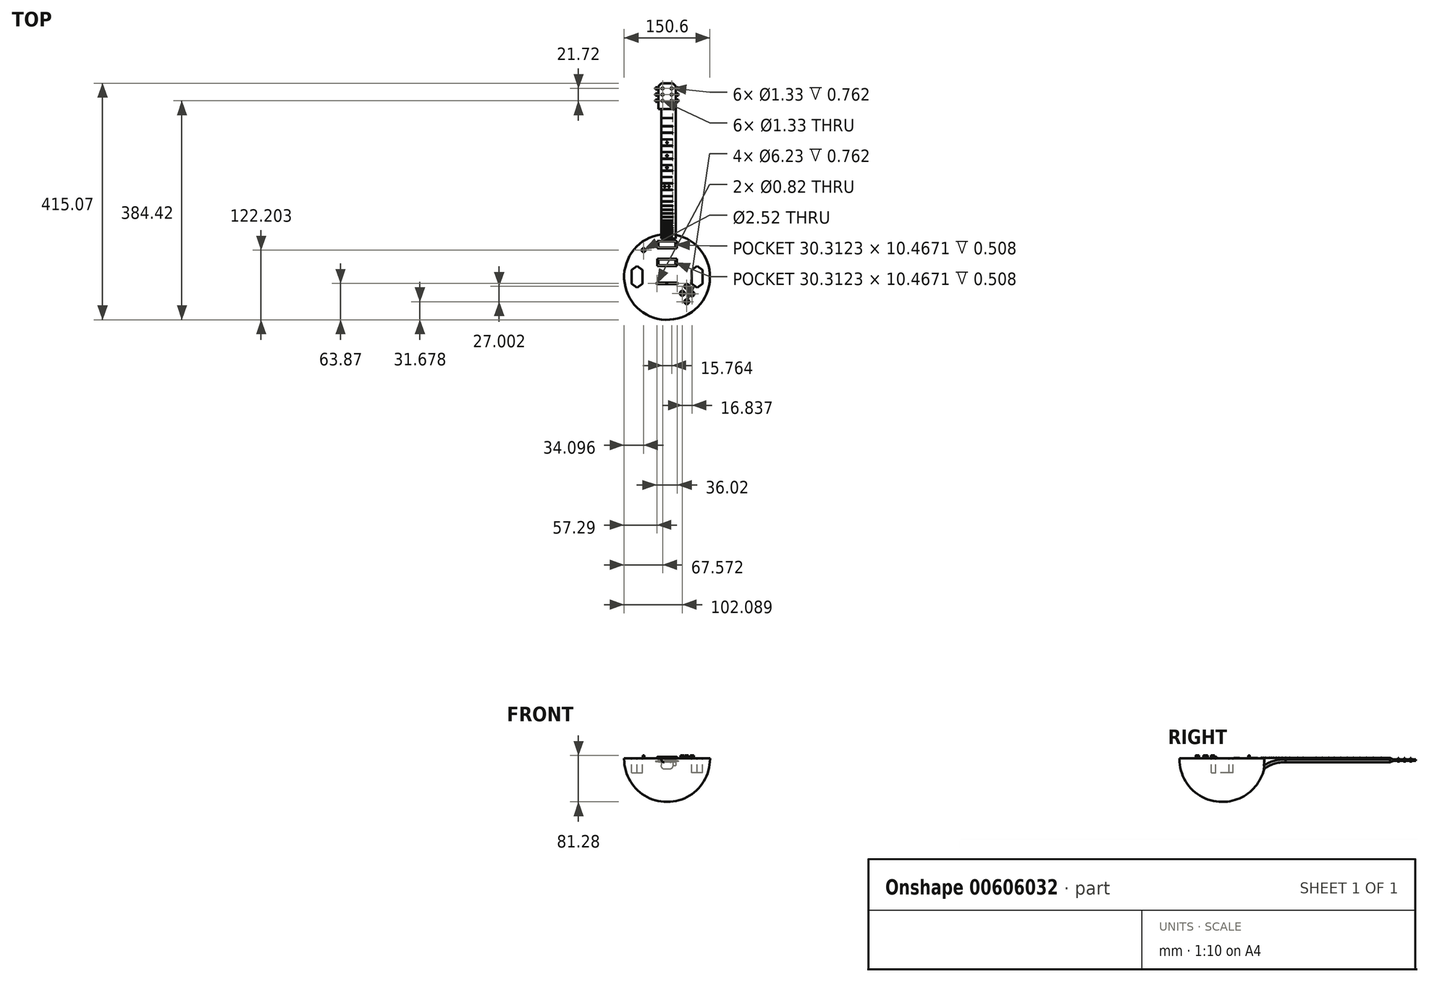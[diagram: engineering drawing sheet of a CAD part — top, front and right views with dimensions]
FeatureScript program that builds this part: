
annotation { "Feature Type Name" : "Feature", "Feature Type Description" : "" }
export const myFeature = defineFeature(function(context is Context, id is Id, definition is map)
    precondition{}
    {
        {
            var Q0;
            Q0=qCreatedBy(makeId("Top.planeOp"),FACE);
            var sketch = newSketch(context, id + "F0", { "sketchPlane" : qUnion([Q0])});
            skCircle(sketch, "E0", {"center": v(0, 0) * mm, "radius": 75.3 * mm});
            skSolve(sketch);
        }
        {
            var Q0;
            Q0 = qSketchRegion(id + "F0", true);
            extrude(context, id + "F1", {"entities" : qUnion([Q0]), "oppositeDirection" : true, "depth" : 76.2 * mm, "offsetDistance" : 25.4 * mm});
        }
        {
            var Q0;
            Q0=makeQuery(id+"F1.opExtrude","CAP_EDGE",EDGE,{"disambiguationData":[OSD([sQuery(id+"F0.wireOp",EDGE,"E0")])],"isStart":false});
            fillet(context, id + "F2", {"entities" : qUnion([Q0]), "radius" : 74.93 * mm, "tangentPropagation" : true, "allowEdgeOverflow" : false});
        }
        {
            var Q0;
            Q0=makeQuery(id+"F1.opExtrude","CAP_FACE",FACE,{"disambiguationData":[OSD([sQuery(id+"F0.wireOp",EDGE,"E0")])],"isStart":true});
            var sketch = newSketch(context, id + "F3", { "sketchPlane" : qUnion([Q0])});
            skCircle(sketch, "E1.0", {"center": v(0, 0) * mm, "radius": 75.3 * mm});
            skLineSegment(sketch, "E2", {"start": v(0, 0) * mm, "end": v(-75.3, 0) * mm, "construction": true});
            skLineSegment(sketch, "E3", {"start": v(0, 0) * mm, "end": v(75.3, 0) * mm, "construction": true});
            skLineSegment(sketch, "E4", {"start": v(0, 0) * mm, "end": v(0, 75.3) * mm, "construction": true});
            skLineSegment(sketch, "E5", {"start": v(0, 0) * mm, "end": v(0, -75.3) * mm, "construction": true});
            skLineSegment(sketch, "E6", {"start": v(-62.04, 0) * mm, "end": v(-62.04, 11.91) * mm});
            skLineSegment(sketch, "E7", {"start": v(-62.04, 11.91) * mm, "end": v(-52.65, 18.94) * mm});
            skLineSegment(sketch, "E8", {"start": v(-52.65, 18.94) * mm, "end": v(-43.25, 11.91) * mm});
            skLineSegment(sketch, "E9", {"start": v(-43.25, 11.91) * mm, "end": v(-43.25, 0) * mm});
            skLineSegment(sketch, "E10.MirrorCS", {"start": v(-43.25, -11.91) * mm, "end": v(-43.25, 0) * mm});
            skLineSegment(sketch, "E11.MirrorCS", {"start": v(-52.65, -18.94) * mm, "end": v(-43.25, -11.91) * mm});
            skLineSegment(sketch, "E12.MirrorCS", {"start": v(-62.04, -11.91) * mm, "end": v(-52.65, -18.94) * mm});
            skLineSegment(sketch, "E13.MirrorCS", {"start": v(-62.04, 0) * mm, "end": v(-62.04, -11.91) * mm});
            skLineSegment(sketch, "E14.MirrorCS", {"start": v(43.25, 11.91) * mm, "end": v(43.25, 0) * mm});
            skLineSegment(sketch, "E15.MirrorCS", {"start": v(52.65, 18.94) * mm, "end": v(43.25, 11.91) * mm});
            skLineSegment(sketch, "E16.MirrorCS", {"start": v(62.04, 11.91) * mm, "end": v(52.65, 18.94) * mm});
            skLineSegment(sketch, "E17.MirrorCS", {"start": v(62.04, 0) * mm, "end": v(62.04, 11.91) * mm});
            skLineSegment(sketch, "E18.MirrorCS", {"start": v(62.04, 0) * mm, "end": v(62.04, -11.91) * mm});
            skLineSegment(sketch, "E19.MirrorCS", {"start": v(43.25, -11.91) * mm, "end": v(43.25, 0) * mm});
            skLineSegment(sketch, "E20.MirrorCS", {"start": v(52.65, -18.94) * mm, "end": v(43.25, -11.91) * mm});
            skLineSegment(sketch, "E21.MirrorCS", {"start": v(62.04, -11.91) * mm, "end": v(52.65, -18.94) * mm});
            skLineSegment(sketch, "E22", {"start": v(0, 63) * mm, "end": v(17.31, 63) * mm});
            skLineSegment(sketch, "E23", {"start": v(17.31, 63) * mm, "end": v(17.31, 50.39) * mm});
            skLineSegment(sketch, "E24", {"start": v(17.31, 50.39) * mm, "end": v(0, 50.39) * mm});
            skLineSegment(sketch, "E25", {"start": v(0, 50.39) * mm, "end": v(-17.31, 50.39) * mm});
            skLineSegment(sketch, "E26", {"start": v(-17.31, 50.39) * mm, "end": v(-17.31, 63) * mm});
            skLineSegment(sketch, "E27", {"start": v(-17.31, 63) * mm, "end": v(0, 63) * mm});
            skLineSegment(sketch, "E28", {"start": v(-15.36, 51.52) * mm, "end": v(-15.36, 61.98) * mm});
            skLineSegment(sketch, "E29", {"start": v(-15.36, 61.98) * mm, "end": v(14.95, 61.98) * mm});
            skLineSegment(sketch, "E30", {"start": v(14.95, 61.98) * mm, "end": v(14.95, 51.52) * mm});
            skLineSegment(sketch, "E31", {"start": v(14.95, 51.52) * mm, "end": v(-15.36, 51.52) * mm});
            skCircle(sketch, "E32", {"center": v(-16.46, 60.98) * mm, "radius": 0.48 * mm});
            skCircle(sketch, "E33", {"center": v(-16.46, 57.1) * mm, "radius": 0.48 * mm});
            skCircle(sketch, "E34", {"center": v(-16.46, 52.33) * mm, "radius": 0.48 * mm});
            skCircle(sketch, "E35", {"center": v(16.04, 60.98) * mm, "radius": 0.48 * mm});
            skCircle(sketch, "E36", {"center": v(16.04, 57.1) * mm, "radius": 0.48 * mm});
            skCircle(sketch, "E37", {"center": v(16.04, 52.33) * mm, "radius": 0.48 * mm});
            skLineSegment(sketch, "E38", {"start": v(0, 31.55) * mm, "end": v(17.31, 31.55) * mm});
            skLineSegment(sketch, "E39", {"start": v(17.31, 31.55) * mm, "end": v(17.31, 18.94) * mm});
            skLineSegment(sketch, "E40", {"start": v(17.31, 18.94) * mm, "end": v(0, 18.94) * mm});
            skLineSegment(sketch, "E41", {"start": v(0, 18.94) * mm, "end": v(-17.31, 18.94) * mm});
            skLineSegment(sketch, "E42", {"start": v(-17.31, 18.94) * mm, "end": v(-17.31, 31.55) * mm});
            skLineSegment(sketch, "E43", {"start": v(-17.31, 31.55) * mm, "end": v(0, 31.55) * mm});
            skLineSegment(sketch, "E44", {"start": v(-15.36, 20.07) * mm, "end": v(-15.36, 30.53) * mm});
            skLineSegment(sketch, "E45", {"start": v(-15.36, 30.53) * mm, "end": v(14.95, 30.53) * mm});
            skLineSegment(sketch, "E46", {"start": v(14.95, 30.53) * mm, "end": v(14.95, 20.07) * mm});
            skLineSegment(sketch, "E47", {"start": v(14.95, 20.07) * mm, "end": v(-15.36, 20.07) * mm});
            skCircle(sketch, "E48", {"center": v(-16.46, 29.53) * mm, "radius": 0.48 * mm});
            skCircle(sketch, "E49", {"center": v(-16.46, 25.65) * mm, "radius": 0.48 * mm});
            skCircle(sketch, "E50", {"center": v(-16.46, 20.88) * mm, "radius": 0.48 * mm});
            skCircle(sketch, "E51", {"center": v(16.04, 29.53) * mm, "radius": 0.48 * mm});
            skCircle(sketch, "E52", {"center": v(16.04, 25.65) * mm, "radius": 0.48 * mm});
            skCircle(sketch, "E53", {"center": v(16.04, 20.88) * mm, "radius": 0.48 * mm});
            skLineSegment(sketch, "E54", {"start": v(0, -9.89) * mm, "end": v(17.31, -9.89) * mm});
            skLineSegment(sketch, "E55", {"start": v(17.31, -9.89) * mm, "end": v(17.31, -12.97) * mm});
            skLineSegment(sketch, "E56", {"start": v(17.31, -12.97) * mm, "end": v(0, -12.97) * mm});
            skLineSegment(sketch, "E57.MirrorCS", {"start": v(-17.31, -12.97) * mm, "end": v(0, -12.97) * mm});
            skLineSegment(sketch, "E58.MirrorCS", {"start": v(0, -9.89) * mm, "end": v(-17.31, -9.89) * mm});
            skLineSegment(sketch, "E59.MirrorCS", {"start": v(-17.31, -9.89) * mm, "end": v(-17.31, -12.97) * mm});
            skArc(sketch, "E60", {"start": v(-17.31, -9.89) * mm, "mid": v(-18.85, -11.43) * mm, "end": v(-17.31, -12.97) * mm});
            skArc(sketch, "E61.MirrorCS", {"start": v(17.31, -9.89) * mm, "mid": v(18.85, -11.43) * mm, "end": v(17.31, -12.97) * mm});
            skCircle(sketch, "E62", {"center": v(-18, -11.43) * mm, "radius": 0.41 * mm});
            skCircle(sketch, "E63.MirrorC", {"center": v(18, -11.43) * mm, "radius": 0.41 * mm});
            skCircle(sketch, "E64", {"center": v(34.62, -16.62) * mm, "radius": 4.23 * mm});
            skCircle(sketch, "E65", {"center": v(26.79, -28.94) * mm, "radius": 4.23 * mm});
            skCircle(sketch, "E66", {"center": v(43.63, -29.8) * mm, "radius": 4.23 * mm});
            skCircle(sketch, "E67", {"center": v(34.56, -43.62) * mm, "radius": 4.23 * mm});
            skCircle(sketch, "E68", {"center": v(34.62, -16.62) * mm, "radius": 3.12 * mm});
            skCircle(sketch, "E69", {"center": v(26.79, -28.94) * mm, "radius": 3.12 * mm});
            skCircle(sketch, "E70", {"center": v(43.63, -29.8) * mm, "radius": 3.12 * mm});
            skCircle(sketch, "E71", {"center": v(34.56, -43.62) * mm, "radius": 3.12 * mm});
            skCircle(sketch, "E72", {"center": v(-41.2, 46.9) * mm, "radius": 3.4 * mm});
            skCircle(sketch, "E73", {"center": v(-41.2, 46.9) * mm, "radius": 1.26 * mm});
            skSolve(sketch);
        }
        {
            var Q0;
            Q0=makeQuery(id+"F3.imprint","IMPRINT",FACE,{"disambiguationData":[TD([[makeQuery(id+"F3.imprint","IMPRINT",EDGE,{"derivedFrom":sQuery(id+"F3.wireOp",EDGE,"E6")}),-1.0]])]});
            var Q1;
            Q1=makeQuery(id+"F3.imprint","IMPRINT",FACE,{"disambiguationData":[TD([[makeQuery(id+"F3.imprint","IMPRINT",EDGE,{"derivedFrom":sQuery(id+"F3.wireOp",EDGE,"E14.MirrorCS")}),1.0]])]});
            extrude(context, id + "F4", {"entities" : qUnion([Q0, Q1]), "operationType" : NewBodyOperationType.REMOVE, "oppositeDirection" : true, "depth" : 25.4 * mm, "offsetDistance" : 25.4 * mm});
        }
        {
            var Q0;
            Q0=makeQuery(id+"F3.imprint","IMPRINT",FACE,{"disambiguationData":[TD([[makeQuery(id+"F3.imprint","IMPRINT",EDGE,{"derivedFrom":sQuery(id+"F3.wireOp",EDGE,"E22")}),-1.0]])]});
            var Q1;
            Q1=makeQuery(id+"F3.imprint","IMPRINT",FACE,{"disambiguationData":[TD([[makeQuery(id+"F3.imprint","IMPRINT",EDGE,{"derivedFrom":sQuery(id+"F3.wireOp",EDGE,"E38")}),-1.0]])]});
            extrude(context, id + "F5", {"entities" : qUnion([Q0, Q1]), "depth" : 0.5 * mm, "offsetDistance" : 25.4 * mm});
        }
        {
            var Q0;
            Q0=makeQuery(id+"F3.imprint","IMPRINT",FACE,{"disambiguationData":[TD([[makeQuery(id+"F3.imprint","IMPRINT",EDGE,{"derivedFrom":sQuery(id+"F3.wireOp",EDGE,"E32")}),1.0]])]});
            extrude(context, id + "F6", {"entities" : qUnion([Q0]), "depth" : 0.76 * mm, "offsetDistance" : 25.4 * mm});
        }
        {
            var Q0;
            Q0=makeQuery(id+"F3.imprint","IMPRINT",FACE,{"disambiguationData":[TD([[makeQuery(id+"F3.imprint","IMPRINT",EDGE,{"derivedFrom":sQuery(id+"F3.wireOp",EDGE,"E33")}),1.0]])]});
            var Q1;
            Q1=makeQuery(id+"F3.imprint","IMPRINT",FACE,{"disambiguationData":[TD([[makeQuery(id+"F3.imprint","IMPRINT",EDGE,{"derivedFrom":sQuery(id+"F3.wireOp",EDGE,"E34")}),1.0]])]});
            var Q2;
            Q2=makeQuery(id+"F3.imprint","IMPRINT",FACE,{"disambiguationData":[TD([[makeQuery(id+"F3.imprint","IMPRINT",EDGE,{"derivedFrom":sQuery(id+"F3.wireOp",EDGE,"E35")}),1.0]])]});
            var Q3;
            Q3=makeQuery(id+"F3.imprint","IMPRINT",FACE,{"disambiguationData":[TD([[makeQuery(id+"F3.imprint","IMPRINT",EDGE,{"derivedFrom":sQuery(id+"F3.wireOp",EDGE,"E36")}),1.0]])]});
            var Q4;
            Q4=makeQuery(id+"F3.imprint","IMPRINT",FACE,{"disambiguationData":[TD([[makeQuery(id+"F3.imprint","IMPRINT",EDGE,{"derivedFrom":sQuery(id+"F3.wireOp",EDGE,"E37")}),1.0]])]});
            var Q5;
            Q5=makeQuery(id+"F3.imprint","IMPRINT",FACE,{"disambiguationData":[TD([[makeQuery(id+"F3.imprint","IMPRINT",EDGE,{"derivedFrom":sQuery(id+"F3.wireOp",EDGE,"E48")}),1.0]])]});
            var Q6;
            Q6=makeQuery(id+"F3.imprint","IMPRINT",FACE,{"disambiguationData":[TD([[makeQuery(id+"F3.imprint","IMPRINT",EDGE,{"derivedFrom":sQuery(id+"F3.wireOp",EDGE,"E49")}),1.0]])]});
            var Q7;
            Q7=makeQuery(id+"F3.imprint","IMPRINT",FACE,{"disambiguationData":[TD([[makeQuery(id+"F3.imprint","IMPRINT",EDGE,{"derivedFrom":sQuery(id+"F3.wireOp",EDGE,"E50")}),1.0]])]});
            var Q8;
            Q8=makeQuery(id+"F3.imprint","IMPRINT",FACE,{"disambiguationData":[TD([[makeQuery(id+"F3.imprint","IMPRINT",EDGE,{"derivedFrom":sQuery(id+"F3.wireOp",EDGE,"E51")}),1.0]])]});
            var Q9;
            Q9=makeQuery(id+"F3.imprint","IMPRINT",FACE,{"disambiguationData":[TD([[makeQuery(id+"F3.imprint","IMPRINT",EDGE,{"derivedFrom":sQuery(id+"F3.wireOp",EDGE,"E52")}),1.0]])]});
            var Q10;
            Q10=makeQuery(id+"F3.imprint","IMPRINT",FACE,{"disambiguationData":[TD([[makeQuery(id+"F3.imprint","IMPRINT",EDGE,{"derivedFrom":sQuery(id+"F3.wireOp",EDGE,"E53")}),1.0]])]});
            extrude(context, id + "F7", {"entities" : qUnion([Q0, Q1, Q2, Q3, Q4, Q5, Q6, Q7, Q8, Q9, Q10]), "operationType" : NewBodyOperationType.ADD, "depth" : 0.76 * mm, "offsetDistance" : 25.4 * mm});
        }
        {
            var Q0;
            Q0=makeQuery(id+"F3.imprint","IMPRINT",FACE,{"disambiguationData":[TD([[makeQuery(id+"F3.imprint","IMPRINT",EDGE,{"derivedFrom":sQuery(id+"F3.wireOp",EDGE,"E44")}),-1.0]])]});
            var Q1;
            Q1=makeQuery(id+"F3.imprint","IMPRINT",FACE,{"disambiguationData":[TD([[makeQuery(id+"F3.imprint","IMPRINT",EDGE,{"derivedFrom":sQuery(id+"F3.wireOp",EDGE,"E28")}),-1.0]])]});
            extrude(context, id + "F8", {"entities" : qUnion([Q0, Q1]), "depth" : 1.02 * mm, "offsetDistance" : 25.4 * mm});
        }
        {
            var Q0;
            Q0=makeQuery(id+"F3.imprint","IMPRINT",FACE,{"disambiguationData":[TD([[makeQuery(id+"F3.imprint","IMPRINT",EDGE,{"derivedFrom":sQuery(id+"F3.wireOp",EDGE,"E54")}),-1.0]])]});
            extrude(context, id + "F9", {"entities" : qUnion([Q0]), "depth" : 2.54 * mm, "offsetDistance" : 25.4 * mm});
        }
        {
            var Q0;
            Q0=makeQuery(id+"F9.opExtrude","CAP_EDGE",EDGE,{"disambiguationData":[OSD([sQuery(id+"F3.wireOp",EDGE,"E56"),sQuery(id+"F3.wireOp",EDGE,"E57.MirrorCS")])],"isStart":false});
            fillet(context, id + "F10", {"entities" : qUnion([Q0]), "radius" : 3.05 * mm, "tangentPropagation" : true, "allowEdgeOverflow" : false});
        }
        {
            var Q0;
            Q0=makeQuery(id+"F3.imprint","IMPRINT",FACE,{"disambiguationData":[TD([[makeQuery(id+"F3.imprint","IMPRINT",EDGE,{"derivedFrom":sQuery(id+"F3.wireOp",EDGE,"E59.MirrorCS")}),-1.0]])]});
            var Q1;
            Q1=makeQuery(id+"F3.imprint","IMPRINT",FACE,{"disambiguationData":[TD([[makeQuery(id+"F3.imprint","IMPRINT",EDGE,{"derivedFrom":sQuery(id+"F3.wireOp",EDGE,"E55")}),1.0]])]});
            extrude(context, id + "F11", {"entities" : qUnion([Q0, Q1]), "depth" : 0.5 * mm, "offsetDistance" : 25.4 * mm});
        }
        {
            var Q0;
            Q0=makeQuery(id+"F3.imprint","IMPRINT",FACE,{"disambiguationData":[TD([[makeQuery(id+"F3.imprint","IMPRINT",EDGE,{"derivedFrom":sQuery(id+"F3.wireOp",EDGE,"E65")}),1.0]])]});
            var Q1;
            Q1=makeQuery(id+"F3.imprint","IMPRINT",FACE,{"disambiguationData":[TD([[makeQuery(id+"F3.imprint","IMPRINT",EDGE,{"derivedFrom":sQuery(id+"F3.wireOp",EDGE,"E64")}),1.0]])]});
            var Q2;
            Q2=makeQuery(id+"F3.imprint","IMPRINT",FACE,{"disambiguationData":[TD([[makeQuery(id+"F3.imprint","IMPRINT",EDGE,{"derivedFrom":sQuery(id+"F3.wireOp",EDGE,"E66")}),1.0]])]});
            var Q3;
            Q3=makeQuery(id+"F3.imprint","IMPRINT",FACE,{"disambiguationData":[TD([[makeQuery(id+"F3.imprint","IMPRINT",EDGE,{"derivedFrom":sQuery(id+"F3.wireOp",EDGE,"E67")}),1.0]])]});
            extrude(context, id + "F12", {"entities" : qUnion([Q0, Q1, Q2, Q3]), "depth" : 0.76 * mm, "offsetDistance" : 25.4 * mm});
        }
        {
            var Q0;
            Q0=makeQuery(id+"F3.imprint","IMPRINT",FACE,{"disambiguationData":[TD([[makeQuery(id+"F3.imprint","IMPRINT",EDGE,{"derivedFrom":sQuery(id+"F3.wireOp",EDGE,"E69")}),1.0]])]});
            var Q1;
            Q1=makeQuery(id+"F3.imprint","IMPRINT",FACE,{"disambiguationData":[TD([[makeQuery(id+"F3.imprint","IMPRINT",EDGE,{"derivedFrom":sQuery(id+"F3.wireOp",EDGE,"E68")}),1.0]])]});
            var Q2;
            Q2=makeQuery(id+"F3.imprint","IMPRINT",FACE,{"disambiguationData":[TD([[makeQuery(id+"F3.imprint","IMPRINT",EDGE,{"derivedFrom":sQuery(id+"F3.wireOp",EDGE,"E70")}),1.0]])]});
            var Q3;
            Q3=makeQuery(id+"F3.imprint","IMPRINT",FACE,{"disambiguationData":[TD([[makeQuery(id+"F3.imprint","IMPRINT",EDGE,{"derivedFrom":sQuery(id+"F3.wireOp",EDGE,"E71")}),1.0]])]});
            extrude(context, id + "F13", {"entities" : qUnion([Q0, Q1, Q2, Q3]), "depth" : 5.08 * mm, "offsetDistance" : 25.4 * mm});
        }
        {
            var Q0;
            Q0=makeQuery(id+"F3.imprint","IMPRINT",FACE,{"disambiguationData":[TD([[makeQuery(id+"F3.imprint","IMPRINT",EDGE,{"derivedFrom":sQuery(id+"F3.wireOp",EDGE,"E72")}),1.0]])]});
            extrude(context, id + "F14", {"entities" : qUnion([Q0]), "depth" : 0.76 * mm, "offsetDistance" : 25.4 * mm});
        }
        {
            var Q0;
            Q0=makeQuery(id+"F3.imprint","IMPRINT",FACE,{"disambiguationData":[TD([[makeQuery(id+"F3.imprint","IMPRINT",EDGE,{"derivedFrom":sQuery(id+"F3.wireOp",EDGE,"E73")}),1.0]])]});
            extrude(context, id + "F15", {"entities" : qUnion([Q0]), "depth" : 5.08 * mm, "offsetDistance" : 25.4 * mm});
        }
        {
            var Q0;
            Q0=makeQuery(id+"F15.opExtrude","CAP_EDGE",EDGE,{"disambiguationData":[OSD([sQuery(id+"F3.wireOp",EDGE,"E73")])],"isStart":false});
            fillet(context, id + "F16", {"entities" : qUnion([Q0]), "radius" : 0.5 * mm, "tangentPropagation" : true, "allowEdgeOverflow" : false});
        }
        {
            var Q0;
            Q0=qCreatedBy(makeId("Right.planeOp"),FACE);
            var sketch = newSketch(context, id + "F17", { "sketchPlane" : qUnion([Q0])});
            skLineSegment(sketch, "E74", {"start": v(67.16, 0) * mm, "end": v(294.63, 0) * mm});
            skArc(sketch, "E75", {"start": v(110.96, -6.75) * mm, "mid": v(85.61, -11.39) * mm, "end": v(64.76, -26.52) * mm});
            skLineSegment(sketch, "E76", {"start": v(64.76, -26.52) * mm, "end": v(67.16, 0) * mm});
            skLineSegment(sketch, "E77", {"start": v(110.96, -6.75) * mm, "end": v(294.63, -6.75) * mm});
            skLineSegment(sketch, "E78", {"start": v(294.63, -6.75) * mm, "end": v(294.63, 0) * mm});
            skSolve(sketch);
        }
        {
            var Q0;
            Q0=makeQuery(id+"F17.imprint","IMPRINT",FACE,{"disambiguationData":[TD([[makeQuery(id+"F17.imprint","IMPRINT",EDGE,{"derivedFrom":sQuery(id+"F17.wireOp",EDGE,"E74")}),-1.0]])]});
            extrude(context, id + "F18", {"entities" : qUnion([Q0]), "endBound" : BoundingType.SYMMETRIC, "depth" : 20.32 * mm, "offsetDistance" : 25.4 * mm});
        }
        {
            var Q0;
            Q0=makeQuery(id+"F18.opExtrude","CAP_EDGE",EDGE,{"disambiguationData":[OSD([sQuery(id+"F17.wireOp",EDGE,"E77")])],"isStart":false});
            var Q1;
            Q1=makeQuery(id+"F18.opExtrude","CAP_EDGE",EDGE,{"disambiguationData":[OSD([sQuery(id+"F17.wireOp",EDGE,"E77")])],"isStart":true});
            fillet(context, id + "F19", {"entities" : qUnion([Q0, Q1]), "radius" : 5.08 * mm, "tangentPropagation" : true, "allowEdgeOverflow" : false});
        }
        {
            var Q0;
            Q0=makeQuery(id+"F18.opExtrude","SWEPT_FACE",FACE,{"disambiguationData":[OSD([sQuery(id+"F17.wireOp",EDGE,"E74")])]});
            extrude(context, id + "F20", {"entities" : qUnion([Q0]), "depth" : 0.76 * mm, "offsetDistance" : 25.4 * mm});
        }
        {
            var Q0;
            Q0=makeQuery(id+"F20.opExtrude","CAP_FACE",FACE,{"disambiguationData":[OSD([sQuery(id+"F17.wireOp",EDGE,"E74")])],"isStart":false});
            var sketch = newSketch(context, id + "F21", { "sketchPlane" : qUnion([Q0])});
            skLineSegment(sketch, "E79", {"start": v(-10.16, 279.07) * mm, "end": v(10.16, 279.07) * mm});
            skLineSegment(sketch, "E80", {"start": v(10.16, 279.07) * mm, "end": v(10.16, 278.57) * mm});
            skLineSegment(sketch, "E81", {"start": v(10.16, 278.57) * mm, "end": v(-10.16, 278.57) * mm});
            skLineSegment(sketch, "E82", {"start": v(-10.16, 278.57) * mm, "end": v(-10.16, 279.07) * mm});
            skLineSegment(sketch, "E83", {"start": v(-10.16, 264.98) * mm, "end": v(10.16, 264.98) * mm});
            skLineSegment(sketch, "E84", {"start": v(10.16, 264.98) * mm, "end": v(10.16, 264.47) * mm});
            skLineSegment(sketch, "E85", {"start": v(10.16, 264.47) * mm, "end": v(-10.16, 264.47) * mm});
            skLineSegment(sketch, "E86", {"start": v(-10.16, 264.47) * mm, "end": v(-10.16, 264.98) * mm});
            skLineSegment(sketch, "E87", {"start": v(-10.22, 253.13) * mm, "end": v(10.1, 253.13) * mm});
            skLineSegment(sketch, "E88", {"start": v(10.1, 253.13) * mm, "end": v(10.1, 252.63) * mm});
            skLineSegment(sketch, "E89", {"start": v(10.1, 252.63) * mm, "end": v(-10.22, 252.63) * mm});
            skLineSegment(sketch, "E90", {"start": v(-10.22, 252.63) * mm, "end": v(-10.22, 253.13) * mm});
            skLineSegment(sketch, "E91", {"start": v(-10.16, 241.6) * mm, "end": v(10.16, 241.6) * mm});
            skLineSegment(sketch, "E92", {"start": v(10.16, 241.6) * mm, "end": v(10.16, 241.08) * mm});
            skLineSegment(sketch, "E93", {"start": v(10.16, 241.08) * mm, "end": v(-10.16, 241.08) * mm});
            skLineSegment(sketch, "E94", {"start": v(-10.16, 241.08) * mm, "end": v(-10.16, 241.6) * mm});
            skLineSegment(sketch, "E95", {"start": v(-10.16, 230.3) * mm, "end": v(9.79, 230.3) * mm});
            skLineSegment(sketch, "E96", {"start": v(9.79, 230.3) * mm, "end": v(9.79, 229.8) * mm});
            skLineSegment(sketch, "E97", {"start": v(9.79, 229.8) * mm, "end": v(-10.16, 229.8) * mm});
            skLineSegment(sketch, "E98", {"start": v(-10.16, 229.8) * mm, "end": v(-10.16, 230.3) * mm});
            skLineSegment(sketch, "E99", {"start": v(-10.22, 219.37) * mm, "end": v(10.1, 219.37) * mm});
            skLineSegment(sketch, "E100", {"start": v(10.1, 219.37) * mm, "end": v(10.1, 218.86) * mm});
            skLineSegment(sketch, "E101", {"start": v(10.1, 218.86) * mm, "end": v(-10.22, 218.86) * mm});
            skLineSegment(sketch, "E102", {"start": v(-10.22, 218.86) * mm, "end": v(-10.22, 219.37) * mm});
            skLineSegment(sketch, "E103", {"start": v(-10.16, 207.82) * mm, "end": v(10.16, 207.82) * mm});
            skLineSegment(sketch, "E104", {"start": v(10.16, 207.82) * mm, "end": v(10.16, 207.32) * mm});
            skLineSegment(sketch, "E105", {"start": v(10.16, 207.32) * mm, "end": v(-10.16, 207.32) * mm});
            skLineSegment(sketch, "E106", {"start": v(-10.16, 207.32) * mm, "end": v(-10.16, 207.82) * mm});
            skLineSegment(sketch, "E107", {"start": v(-10.16, 196.53) * mm, "end": v(9.79, 196.53) * mm});
            skLineSegment(sketch, "E108", {"start": v(9.79, 196.53) * mm, "end": v(9.79, 196.03) * mm});
            skLineSegment(sketch, "E109", {"start": v(9.79, 196.03) * mm, "end": v(-10.16, 196.03) * mm});
            skLineSegment(sketch, "E110", {"start": v(-10.16, 196.03) * mm, "end": v(-10.16, 196.53) * mm});
            skLineSegment(sketch, "E111", {"start": v(-10.16, 186.9) * mm, "end": v(10.16, 186.9) * mm});
            skLineSegment(sketch, "E112", {"start": v(10.16, 186.9) * mm, "end": v(10.16, 186.4) * mm});
            skLineSegment(sketch, "E113", {"start": v(10.16, 186.4) * mm, "end": v(-10.16, 186.4) * mm});
            skLineSegment(sketch, "E114", {"start": v(-10.16, 186.4) * mm, "end": v(-10.16, 186.9) * mm});
            skLineSegment(sketch, "E115", {"start": v(-10.16, 175.61) * mm, "end": v(9.79, 175.61) * mm});
            skLineSegment(sketch, "E116", {"start": v(9.79, 175.61) * mm, "end": v(9.79, 175.1) * mm});
            skLineSegment(sketch, "E117", {"start": v(9.79, 175.1) * mm, "end": v(-10.16, 175.1) * mm});
            skLineSegment(sketch, "E118", {"start": v(-10.16, 175.1) * mm, "end": v(-10.16, 175.61) * mm});
            skLineSegment(sketch, "E119", {"start": v(-10.22, 164.68) * mm, "end": v(10.1, 164.68) * mm});
            skLineSegment(sketch, "E120", {"start": v(10.1, 164.68) * mm, "end": v(10.1, 164.17) * mm});
            skLineSegment(sketch, "E121", {"start": v(10.1, 164.17) * mm, "end": v(-10.22, 164.17) * mm});
            skLineSegment(sketch, "E122", {"start": v(-10.22, 164.17) * mm, "end": v(-10.22, 164.68) * mm});
            skLineSegment(sketch, "E123", {"start": v(-10.16, 153.13) * mm, "end": v(10.16, 153.13) * mm});
            skLineSegment(sketch, "E124", {"start": v(10.16, 153.13) * mm, "end": v(10.16, 152.63) * mm});
            skLineSegment(sketch, "E125", {"start": v(10.16, 152.63) * mm, "end": v(-10.16, 152.63) * mm});
            skLineSegment(sketch, "E126", {"start": v(-10.16, 152.63) * mm, "end": v(-10.16, 153.13) * mm});
            skLineSegment(sketch, "E127", {"start": v(-10.16, 141.84) * mm, "end": v(10.16, 141.86) * mm});
            skLineSegment(sketch, "E128", {"start": v(10.16, 141.86) * mm, "end": v(10.16, 141.34) * mm});
            skLineSegment(sketch, "E129", {"start": v(10.16, 141.34) * mm, "end": v(-10.16, 141.34) * mm});
            skLineSegment(sketch, "E130", {"start": v(-10.16, 141.34) * mm, "end": v(-10.16, 141.84) * mm});
            skLineSegment(sketch, "E131", {"start": v(-10.16, 132.63) * mm, "end": v(10.16, 132.63) * mm});
            skLineSegment(sketch, "E132", {"start": v(10.16, 132.63) * mm, "end": v(10.16, 132.12) * mm});
            skLineSegment(sketch, "E133", {"start": v(10.16, 132.12) * mm, "end": v(-10.16, 132.12) * mm});
            skLineSegment(sketch, "E134", {"start": v(-10.16, 132.12) * mm, "end": v(-10.16, 132.63) * mm});
            skLineSegment(sketch, "E135", {"start": v(-10.16, 125.2) * mm, "end": v(10.15, 125.2) * mm});
            skLineSegment(sketch, "E136", {"start": v(10.15, 125.2) * mm, "end": v(10.15, 124.7) * mm});
            skLineSegment(sketch, "E137", {"start": v(10.15, 124.7) * mm, "end": v(-10.16, 124.7) * mm});
            skLineSegment(sketch, "E138", {"start": v(-10.16, 124.7) * mm, "end": v(-10.16, 125.2) * mm});
            skLineSegment(sketch, "E139", {"start": v(-10.16, 118.3) * mm, "end": v(10.12, 118.3) * mm});
            skLineSegment(sketch, "E140", {"start": v(10.12, 118.3) * mm, "end": v(10.12, 117.79) * mm});
            skLineSegment(sketch, "E141", {"start": v(10.12, 117.79) * mm, "end": v(-10.16, 117.79) * mm});
            skLineSegment(sketch, "E142", {"start": v(-10.16, 117.79) * mm, "end": v(-10.16, 118.3) * mm});
            skLineSegment(sketch, "E143", {"start": v(-10.16, 111.69) * mm, "end": v(10.1, 111.69) * mm});
            skLineSegment(sketch, "E144", {"start": v(10.1, 111.69) * mm, "end": v(10.1, 111.18) * mm});
            skLineSegment(sketch, "E145", {"start": v(10.1, 111.18) * mm, "end": v(-10.16, 111.18) * mm});
            skLineSegment(sketch, "E146", {"start": v(-10.16, 111.18) * mm, "end": v(-10.16, 111.69) * mm});
            skLineSegment(sketch, "E147", {"start": v(-10.16, 105.26) * mm, "end": v(10.14, 105.26) * mm});
            skLineSegment(sketch, "E148", {"start": v(10.14, 105.26) * mm, "end": v(10.14, 104.75) * mm});
            skLineSegment(sketch, "E149", {"start": v(10.14, 104.75) * mm, "end": v(-10.16, 104.75) * mm});
            skLineSegment(sketch, "E150", {"start": v(-10.16, 104.75) * mm, "end": v(-10.16, 105.26) * mm});
            skLineSegment(sketch, "E151", {"start": v(-10.16, 99.4) * mm, "end": v(10.14, 99.4) * mm});
            skLineSegment(sketch, "E152", {"start": v(10.14, 99.4) * mm, "end": v(10.14, 98.9) * mm});
            skLineSegment(sketch, "E153", {"start": v(10.14, 98.9) * mm, "end": v(-10.16, 98.9) * mm});
            skLineSegment(sketch, "E154", {"start": v(-10.16, 98.9) * mm, "end": v(-10.16, 99.4) * mm});
            skLineSegment(sketch, "E155", {"start": v(-10.16, 94.82) * mm, "end": v(10.14, 94.82) * mm});
            skLineSegment(sketch, "E156", {"start": v(10.14, 94.82) * mm, "end": v(10.14, 94.31) * mm});
            skLineSegment(sketch, "E157", {"start": v(10.14, 94.31) * mm, "end": v(-10.16, 94.31) * mm});
            skLineSegment(sketch, "E158", {"start": v(-10.16, 94.31) * mm, "end": v(-10.16, 94.82) * mm});
            skLineSegment(sketch, "E159", {"start": v(-10.16, 90.1) * mm, "end": v(10.14, 90.1) * mm});
            skLineSegment(sketch, "E160", {"start": v(10.14, 90.1) * mm, "end": v(10.14, 89.6) * mm});
            skLineSegment(sketch, "E161", {"start": v(10.14, 89.6) * mm, "end": v(-10.16, 89.6) * mm});
            skLineSegment(sketch, "E162", {"start": v(-10.16, 89.6) * mm, "end": v(-10.16, 90.1) * mm});
            skLineSegment(sketch, "E163", {"start": v(-10.16, 86.34) * mm, "end": v(10.14, 86.34) * mm});
            skLineSegment(sketch, "E164", {"start": v(10.14, 86.34) * mm, "end": v(10.14, 85.83) * mm});
            skLineSegment(sketch, "E165", {"start": v(10.14, 85.83) * mm, "end": v(-10.16, 85.83) * mm});
            skLineSegment(sketch, "E166", {"start": v(-10.16, 85.83) * mm, "end": v(-10.16, 86.34) * mm});
            skLineSegment(sketch, "E167", {"start": v(-10.16, 82.7) * mm, "end": v(10.14, 82.7) * mm});
            skLineSegment(sketch, "E168", {"start": v(10.14, 82.7) * mm, "end": v(10.14, 82.2) * mm});
            skLineSegment(sketch, "E169", {"start": v(10.14, 82.2) * mm, "end": v(-10.16, 82.2) * mm});
            skLineSegment(sketch, "E170", {"start": v(-10.16, 82.2) * mm, "end": v(-10.16, 82.7) * mm});
            skLineSegment(sketch, "E171", {"start": v(-10.16, 79.4) * mm, "end": v(10.14, 79.4) * mm});
            skLineSegment(sketch, "E172", {"start": v(10.14, 79.4) * mm, "end": v(10.14, 78.89) * mm});
            skLineSegment(sketch, "E173", {"start": v(10.14, 78.89) * mm, "end": v(-10.16, 78.89) * mm});
            skLineSegment(sketch, "E174", {"start": v(-10.16, 78.89) * mm, "end": v(-10.16, 79.4) * mm});
            skLineSegment(sketch, "E175", {"start": v(-10.16, 76.11) * mm, "end": v(10.14, 76.11) * mm});
            skLineSegment(sketch, "E176", {"start": v(10.14, 76.11) * mm, "end": v(10.14, 75.6) * mm});
            skLineSegment(sketch, "E177", {"start": v(10.14, 75.6) * mm, "end": v(-10.16, 75.6) * mm});
            skLineSegment(sketch, "E178", {"start": v(-10.16, 75.6) * mm, "end": v(-10.16, 76.11) * mm});
            skLineSegment(sketch, "E179", {"start": v(-10.16, 72.64) * mm, "end": v(10.14, 72.64) * mm});
            skLineSegment(sketch, "E180", {"start": v(10.14, 72.64) * mm, "end": v(10.14, 72.13) * mm});
            skLineSegment(sketch, "E181", {"start": v(10.14, 72.13) * mm, "end": v(-10.16, 72.13) * mm});
            skLineSegment(sketch, "E182", {"start": v(-10.16, 72.13) * mm, "end": v(-10.16, 72.64) * mm});
            skLineSegment(sketch, "E183", {"start": v(-10.16, 69.49) * mm, "end": v(10.14, 69.49) * mm});
            skLineSegment(sketch, "E184", {"start": v(10.14, 69.49) * mm, "end": v(10.14, 68.98) * mm});
            skLineSegment(sketch, "E185", {"start": v(10.14, 68.98) * mm, "end": v(-10.16, 68.98) * mm});
            skLineSegment(sketch, "E186", {"start": v(-10.16, 68.98) * mm, "end": v(-10.16, 69.49) * mm});
            skSolve(sketch);
        }
        {
            var Q0;
            Q0 = qSketchRegion(id + "F21", true);
            extrude(context, id + "F22", {"entities" : qUnion([Q0]), "depth" : 0.76 * mm, "offsetDistance" : 25.4 * mm});
        }
        {
            var Q0;
            Q0=makeQuery(id+"F20.opExtrude","CAP_FACE",FACE,{"disambiguationData":[OSD([sQuery(id+"F17.wireOp",EDGE,"E74")])],"isStart":false});
            var sketch = newSketch(context, id + "F23", { "sketchPlane" : qUnion([Q0])});
            skCircle(sketch, "E187", {"center": v(0, 235.8) * mm, "radius": 1.27 * mm});
            skCircle(sketch, "E188", {"center": v(0, 212.69) * mm, "radius": 1.55 * mm});
            skCircle(sketch, "E189", {"center": v(0, 191.83) * mm, "radius": 1.61 * mm});
            skCircle(sketch, "E190", {"center": v(-4.15, 158.59) * mm, "radius": 1.4 * mm});
            skCircle(sketch, "E191", {"center": v(3.44, 158.59) * mm, "radius": 1.4 * mm});
            skSolve(sketch);
        }
        {
            var Q0;
            Q0=makeQuery(id+"F23.imprint","IMPRINT",FACE,{"disambiguationData":[TD([[makeQuery(id+"F23.imprint","IMPRINT",EDGE,{"derivedFrom":sQuery(id+"F23.wireOp",EDGE,"E191")}),1.0]])]});
            var Q1;
            Q1=makeQuery(id+"F23.imprint","IMPRINT",FACE,{"disambiguationData":[TD([[makeQuery(id+"F23.imprint","IMPRINT",EDGE,{"derivedFrom":sQuery(id+"F23.wireOp",EDGE,"E190")}),1.0]])]});
            var Q2;
            Q2=makeQuery(id+"F23.imprint","IMPRINT",FACE,{"disambiguationData":[TD([[makeQuery(id+"F23.imprint","IMPRINT",EDGE,{"derivedFrom":sQuery(id+"F23.wireOp",EDGE,"E189")}),1.0]])]});
            var Q3;
            Q3=makeQuery(id+"F23.imprint","IMPRINT",FACE,{"disambiguationData":[TD([[makeQuery(id+"F23.imprint","IMPRINT",EDGE,{"derivedFrom":sQuery(id+"F23.wireOp",EDGE,"E188")}),1.0]])]});
            var Q4;
            Q4=makeQuery(id+"F23.imprint","IMPRINT",FACE,{"disambiguationData":[TD([[makeQuery(id+"F23.imprint","IMPRINT",EDGE,{"derivedFrom":sQuery(id+"F23.wireOp",EDGE,"E187")}),1.0]])]});
            extrude(context, id + "F24", {"entities" : qUnion([Q0, Q1, Q2, Q3, Q4]), "depth" : 0.25 * mm, "offsetDistance" : 25.4 * mm});
        }
        {
            var Q0;
            Q0=qCreatedBy(makeId("Right.planeOp"),FACE);
            var sketch = newSketch(context, id + "F25", { "sketchPlane" : qUnion([Q0])});
            skLineSegment(sketch, "E192.0.0", {"start": v(294.63, -6.75) * mm, "end": v(294.63, -1.67) * mm});
            skLineSegment(sketch, "E192.0.1", {"start": v(294.63, -6.75) * mm, "end": v(110.96, -6.75) * mm});
            skFitSpline(sketch, "E192.0.2", {"points": [v(110.96, -6.75) * mm, v(110.96, -5.06) * mm, v(110.96, -3.36) * mm, v(110.96, -1.67) * mm]});
            skLineSegment(sketch, "E192.0.3", {"start": v(294.63, -1.67) * mm, "end": v(110.96, -1.67) * mm});
            skLineSegment(sketch, "E193.0", {"start": v(67.16, 0) * mm, "end": v(294.63, 0) * mm});
            skLineSegment(sketch, "E194.0", {"start": v(67.16, 0.76) * mm, "end": v(294.63, 0.76) * mm});
            skPoint(sketch, "E195.0", {"position": v(294.63, -0.84) * mm});
            skLineSegment(sketch, "E196.0", {"start": v(294.63, -1.67) * mm, "end": v(294.63, 0) * mm});
            skLineSegment(sketch, "E197.0", {"start": v(294.63, 0.76) * mm, "end": v(294.63, 0) * mm});
            skLineSegment(sketch, "E198.0.4", {"start": v(294.63, 0) * mm, "end": v(294.63, -1.67) * mm});
            skLineSegment(sketch, "E198.0.5", {"start": v(294.63, -1.67) * mm, "end": v(294.63, -6.75) * mm});
            skLineSegment(sketch, "E199", {"start": v(294.63, 0.76) * mm, "end": v(298.54, -1.25) * mm});
            skLineSegment(sketch, "E200", {"start": v(294.63, -6.75) * mm, "end": v(294.89, -6.6) * mm});
            skLineSegment(sketch, "E201", {"start": v(304.54, -3.97) * mm, "end": v(339.77, -3.97) * mm});
            skLineSegment(sketch, "E202", {"start": v(300.28, -1.67) * mm, "end": v(339.77, -1.67) * mm});
            skLineSegment(sketch, "E203", {"start": v(339.77, -1.67) * mm, "end": v(339.77, -3.97) * mm});
            skPoint(sketch, "E204.visualSharp", {"position": v(299.36, -1.67) * mm});
            skArc(sketch, "E204.filletArc", {"start": v(298.54, -1.25) * mm, "mid": v(299.38, -1.56) * mm, "end": v(300.28, -1.67) * mm});
            skPoint(sketch, "E205.visualSharp", {"position": v(299.36, -3.97) * mm});
            skArc(sketch, "E205.filletArc", {"start": v(304.54, -3.97) * mm, "mid": v(299.54, -4.64) * mm, "end": v(294.89, -6.6) * mm});
            skLineSegment(sketch, "E206", {"start": v(294.63, -6.75) * mm, "end": v(294.63, 0.76) * mm});
            skLineSegment(sketch, "E207", {"start": v(299.54, -4.64) * mm, "end": v(299.54, -1.67) * mm});
            skLineSegment(sketch, "E208", {"start": v(299.54, -1.67) * mm, "end": v(299.54, -1.6) * mm});
            skSolve(sketch);
        }
        {
            var Q0;
            {var subQ1=sQuery(id+"F25.wireOp",EDGE,"E199");Q0=makeQuery(id+"F25.imprint","IMPRINT",FACE,{"disambiguationData":[TD([[makeQuery(id+"F25.imprint","IMPRINT",EDGE,{"derivedFrom":subQ1}),-1.0]])]});}
            var Q1;
            {var subQ3=sQuery(id+"F25.wireOp",EDGE,"E201");Q1=makeQuery(id+"F25.imprint","IMPRINT",FACE,{"disambiguationData":[TD([[makeQuery(id+"F25.imprint","IMPRINT",EDGE,{"derivedFrom":subQ3}),1.0]])]});}
            extrude(context, id + "F26", {"entities" : qUnion([Q0, Q1]), "endBound" : BoundingType.SYMMETRIC, "depth" : 20.32 * mm, "offsetDistance" : 25.4 * mm});
        }
        {
            var Q0;
            Q0=makeQuery(id+"F26.opExtrude","CAP_FACE",FACE,{"disambiguationData":[OSD([sQuery(id+"F25.wireOp",EDGE,"E199"),sQuery(id+"F25.wireOp",EDGE,"E200"),sQuery(id+"F25.wireOp",EDGE,"E201"),sQuery(id+"F25.wireOp",EDGE,"E202"),sQuery(id+"F25.wireOp",EDGE,"E203"),sQuery(id+"F25.wireOp",EDGE,"E204.filletArc"),sQuery(id+"F25.wireOp",EDGE,"E205.filletArc"),sQuery(id+"F25.wireOp",EDGE,"E206")])],"isStart":true});
            extrude(context, id + "F27", {"entities" : qUnion([Q0]), "operationType" : NewBodyOperationType.ADD, "depth" : 5.08 * mm, "offsetDistance" : 25.4 * mm});
        }
        {
            var Q0;
            Q0=makeQuery(id+"F26.opExtrude","CAP_FACE",FACE,{"disambiguationData":[OSD([sQuery(id+"F25.wireOp",EDGE,"E199"),sQuery(id+"F25.wireOp",EDGE,"E200"),sQuery(id+"F25.wireOp",EDGE,"E201"),sQuery(id+"F25.wireOp",EDGE,"E202"),sQuery(id+"F25.wireOp",EDGE,"E203"),sQuery(id+"F25.wireOp",EDGE,"E204.filletArc"),sQuery(id+"F25.wireOp",EDGE,"E205.filletArc"),sQuery(id+"F25.wireOp",EDGE,"E206")])],"isStart":false});
            extrude(context, id + "F28", {"entities" : qUnion([Q0]), "operationType" : NewBodyOperationType.ADD, "depth" : 5.08 * mm, "offsetDistance" : 25.4 * mm});
        }
        {
            var Q0;
            Q0=makeQuery(id+"F27.opExtrude","CAP_EDGE",EDGE,{"disambiguationData":[OSD([sQuery(id+"F25.wireOp",EDGE,"E206")])],"isStart":false});
            var Q1;
            Q1=makeQuery(id+"F28.opExtrude","CAP_EDGE",EDGE,{"disambiguationData":[OSD([sQuery(id+"F25.wireOp",EDGE,"E206")])],"isStart":false});
            var Q2;
            Q2=makeQuery(id+"F28.opExtrude","CAP_EDGE",EDGE,{"disambiguationData":[OSD([sQuery(id+"F25.wireOp",EDGE,"E203")])],"isStart":false});
            var Q3;
            Q3=makeQuery(id+"F27.opExtrude","CAP_EDGE",EDGE,{"disambiguationData":[OSD([sQuery(id+"F25.wireOp",EDGE,"E203")])],"isStart":false});
            chamfer(context, id + "F29", {"entities" : qUnion([Q0, Q1, Q2, Q3]), "width" : 5.08 * mm, "tangentPropagation" : true});
        }
        {
            var Q0;
            {var subQ0=sQuery(id+"F25.wireOp",EDGE,"E202");Q0=makeQuery(id+"F28.boolean.opBoolean","MERGE",FACE,{"derivedFrom":[makeQuery(id+"F27.boolean.opBoolean","MERGE",FACE,{"derivedFrom":[makeQuery(id+"F26.opExtrude","SWEPT_FACE",FACE,{"disambiguationData":[OSD([subQ0])]}),makeQuery(id+"F27.opExtrude","SWEPT_FACE",FACE,{"disambiguationData":[OSD([subQ0])]})]}),makeQuery(id+"F28.opExtrude","SWEPT_FACE",FACE,{"disambiguationData":[OSD([subQ0])]})]});}
            var sketch = newSketch(context, id + "F30", { "sketchPlane" : qUnion([Q0])});
            skCircle(sketch, "E209", {"center": v(8.04, 330.84) * mm, "radius": 1.7 * mm});
            skCircle(sketch, "E210", {"center": v(-7.73, 330.84) * mm, "radius": 1.7 * mm});
            skCircle(sketch, "E211", {"center": v(-7.73, 319.98) * mm, "radius": 1.7 * mm});
            skCircle(sketch, "E212", {"center": v(-7.73, 309.12) * mm, "radius": 1.7 * mm});
            skCircle(sketch, "E213", {"center": v(8.04, 319.98) * mm, "radius": 1.7 * mm});
            skCircle(sketch, "E214", {"center": v(8.04, 309.12) * mm, "radius": 1.7 * mm});
            skCircle(sketch, "E215", {"center": v(-7.73, 330.84) * mm, "radius": 0.67 * mm});
            skCircle(sketch, "E216", {"center": v(8.04, 330.84) * mm, "radius": 0.67 * mm});
            skCircle(sketch, "E217", {"center": v(8.04, 319.98) * mm, "radius": 0.67 * mm});
            skCircle(sketch, "E218", {"center": v(-7.73, 319.98) * mm, "radius": 0.67 * mm});
            skCircle(sketch, "E219", {"center": v(-7.73, 309.12) * mm, "radius": 0.67 * mm});
            skCircle(sketch, "E220", {"center": v(8.04, 309.12) * mm, "radius": 0.67 * mm});
            skSolve(sketch);
        }
        {
            var Q0;
            Q0=makeQuery(id+"F30.imprint","IMPRINT",FACE,{"disambiguationData":[TD([[makeQuery(id+"F30.imprint","IMPRINT",EDGE,{"derivedFrom":sQuery(id+"F30.wireOp",EDGE,"E210")}),1.0]])]});
            var Q1;
            Q1=makeQuery(id+"F30.imprint","IMPRINT",FACE,{"disambiguationData":[TD([[makeQuery(id+"F30.imprint","IMPRINT",EDGE,{"derivedFrom":sQuery(id+"F30.wireOp",EDGE,"E209")}),1.0]])]});
            var Q2;
            Q2=makeQuery(id+"F30.imprint","IMPRINT",FACE,{"disambiguationData":[TD([[makeQuery(id+"F30.imprint","IMPRINT",EDGE,{"derivedFrom":sQuery(id+"F30.wireOp",EDGE,"E213")}),1.0]])]});
            var Q3;
            Q3=makeQuery(id+"F30.imprint","IMPRINT",FACE,{"disambiguationData":[TD([[makeQuery(id+"F30.imprint","IMPRINT",EDGE,{"derivedFrom":sQuery(id+"F30.wireOp",EDGE,"E211")}),1.0]])]});
            var Q4;
            Q4=makeQuery(id+"F30.imprint","IMPRINT",FACE,{"disambiguationData":[TD([[makeQuery(id+"F30.imprint","IMPRINT",EDGE,{"derivedFrom":sQuery(id+"F30.wireOp",EDGE,"E212")}),1.0]])]});
            var Q5;
            Q5=makeQuery(id+"F30.imprint","IMPRINT",FACE,{"disambiguationData":[TD([[makeQuery(id+"F30.imprint","IMPRINT",EDGE,{"derivedFrom":sQuery(id+"F30.wireOp",EDGE,"E214")}),1.0]])]});
            extrude(context, id + "F31", {"entities" : qUnion([Q0, Q1, Q2, Q3, Q4, Q5]), "depth" : 0.5 * mm, "offsetDistance" : 25.4 * mm});
        }
        {
            var Q0;
            Q0=makeQuery(id+"F30.imprint","IMPRINT",FACE,{"disambiguationData":[TD([[makeQuery(id+"F30.imprint","IMPRINT",EDGE,{"derivedFrom":sQuery(id+"F30.wireOp",EDGE,"E215")}),1.0]])]});
            var Q1;
            Q1=makeQuery(id+"F30.imprint","IMPRINT",FACE,{"disambiguationData":[TD([[makeQuery(id+"F30.imprint","IMPRINT",EDGE,{"derivedFrom":sQuery(id+"F30.wireOp",EDGE,"E216")}),1.0]])]});
            var Q2;
            Q2=makeQuery(id+"F30.imprint","IMPRINT",FACE,{"disambiguationData":[TD([[makeQuery(id+"F30.imprint","IMPRINT",EDGE,{"derivedFrom":sQuery(id+"F30.wireOp",EDGE,"E218")}),1.0]])]});
            var Q3;
            Q3=makeQuery(id+"F30.imprint","IMPRINT",FACE,{"disambiguationData":[TD([[makeQuery(id+"F30.imprint","IMPRINT",EDGE,{"derivedFrom":sQuery(id+"F30.wireOp",EDGE,"E217")}),1.0]])]});
            var Q4;
            Q4=makeQuery(id+"F30.imprint","IMPRINT",FACE,{"disambiguationData":[TD([[makeQuery(id+"F30.imprint","IMPRINT",EDGE,{"derivedFrom":sQuery(id+"F30.wireOp",EDGE,"E219")}),1.0]])]});
            var Q5;
            Q5=makeQuery(id+"F30.imprint","IMPRINT",FACE,{"disambiguationData":[TD([[makeQuery(id+"F30.imprint","IMPRINT",EDGE,{"derivedFrom":sQuery(id+"F30.wireOp",EDGE,"E220")}),1.0]])]});
            extrude(context, id + "F32", {"entities" : qUnion([Q0, Q1, Q2, Q3, Q4, Q5]), "depth" : 2.54 * mm, "offsetDistance" : 25.4 * mm});
        }
        {
            var Q0;
            {var subQ0=sQuery(id+"F25.wireOp",EDGE,"E201");Q0=makeQuery(id+"F28.boolean.opBoolean","MERGE",FACE,{"derivedFrom":[makeQuery(id+"F27.boolean.opBoolean","MERGE",FACE,{"derivedFrom":[makeQuery(id+"F26.opExtrude","SWEPT_FACE",FACE,{"disambiguationData":[OSD([subQ0])]}),makeQuery(id+"F27.opExtrude","SWEPT_FACE",FACE,{"disambiguationData":[OSD([subQ0])]})]}),makeQuery(id+"F28.opExtrude","SWEPT_FACE",FACE,{"disambiguationData":[OSD([subQ0])]})]});}
            var sketch = newSketch(context, id + "F33", { "sketchPlane" : qUnion([Q0])});
            skCircle(sketch, "E221.0", {"center": v(8.04, -330.84) * mm, "radius": 0.67 * mm});
            skCircle(sketch, "E222.0", {"center": v(-7.73, -330.84) * mm, "radius": 0.67 * mm});
            skCircle(sketch, "E223.0", {"center": v(-7.73, -319.98) * mm, "radius": 0.67 * mm});
            skCircle(sketch, "E224.0", {"center": v(8.04, -319.98) * mm, "radius": 0.67 * mm});
            skCircle(sketch, "E225.0", {"center": v(8.04, -309.12) * mm, "radius": 0.67 * mm});
            skCircle(sketch, "E226.0", {"center": v(-7.73, -309.12) * mm, "radius": 0.67 * mm});
            skLineSegment(sketch, "E227", {"start": v(8.23, -321.33) * mm, "end": v(9.9, -321.33) * mm});
            skLineSegment(sketch, "E228", {"start": v(9.9, -321.33) * mm, "end": v(9.9, -318.28) * mm});
            skLineSegment(sketch, "E229", {"start": v(9.9, -318.28) * mm, "end": v(6.1, -318.28) * mm});
            skLineSegment(sketch, "E230", {"start": v(6.1, -318.28) * mm, "end": v(6.1, -321.33) * mm});
            skLineSegment(sketch, "E231", {"start": v(6.1, -321.33) * mm, "end": v(8.23, -321.33) * mm});
            skLineSegment(sketch, "E232", {"start": v(8.1, -332.04) * mm, "end": v(9.76, -332.04) * mm});
            skLineSegment(sketch, "E233", {"start": v(9.76, -332.04) * mm, "end": v(9.76, -329) * mm});
            skLineSegment(sketch, "E234", {"start": v(9.76, -329) * mm, "end": v(5.97, -329) * mm});
            skLineSegment(sketch, "E235", {"start": v(5.97, -329) * mm, "end": v(5.97, -332.04) * mm});
            skLineSegment(sketch, "E236", {"start": v(5.97, -332.04) * mm, "end": v(8.1, -332.04) * mm});
            skLineSegment(sketch, "E237", {"start": v(8.07, -310.45) * mm, "end": v(9.73, -310.45) * mm});
            skLineSegment(sketch, "E238", {"start": v(9.73, -310.45) * mm, "end": v(9.73, -307.4) * mm});
            skLineSegment(sketch, "E239", {"start": v(9.73, -307.4) * mm, "end": v(5.94, -307.4) * mm});
            skLineSegment(sketch, "E240", {"start": v(5.94, -307.4) * mm, "end": v(5.94, -310.45) * mm});
            skLineSegment(sketch, "E241", {"start": v(5.94, -310.45) * mm, "end": v(8.07, -310.45) * mm});
            skLineSegment(sketch, "E242", {"start": v(-7.8, -331.91) * mm, "end": v(-6.13, -331.91) * mm});
            skLineSegment(sketch, "E243", {"start": v(-6.13, -331.91) * mm, "end": v(-6.13, -328.87) * mm});
            skLineSegment(sketch, "E244", {"start": v(-6.13, -328.87) * mm, "end": v(-9.92, -328.87) * mm});
            skLineSegment(sketch, "E245", {"start": v(-9.92, -328.87) * mm, "end": v(-9.92, -331.91) * mm});
            skLineSegment(sketch, "E246", {"start": v(-9.92, -331.91) * mm, "end": v(-7.8, -331.91) * mm});
            skLineSegment(sketch, "E247", {"start": v(-7.48, -321.2) * mm, "end": v(-5.82, -321.2) * mm});
            skLineSegment(sketch, "E248", {"start": v(-5.82, -321.2) * mm, "end": v(-5.82, -318.16) * mm});
            skLineSegment(sketch, "E249", {"start": v(-5.82, -318.16) * mm, "end": v(-9.61, -318.16) * mm});
            skLineSegment(sketch, "E250", {"start": v(-9.61, -318.16) * mm, "end": v(-9.61, -321.2) * mm});
            skLineSegment(sketch, "E251", {"start": v(-9.61, -321.2) * mm, "end": v(-7.48, -321.2) * mm});
            skLineSegment(sketch, "E252", {"start": v(-7.53, -310.2) * mm, "end": v(-5.87, -310.2) * mm});
            skLineSegment(sketch, "E253", {"start": v(-5.87, -310.2) * mm, "end": v(-5.87, -307.16) * mm});
            skLineSegment(sketch, "E254", {"start": v(-5.87, -307.16) * mm, "end": v(-9.66, -307.16) * mm});
            skLineSegment(sketch, "E255", {"start": v(-9.66, -307.16) * mm, "end": v(-9.66, -310.2) * mm});
            skLineSegment(sketch, "E256", {"start": v(-9.66, -310.2) * mm, "end": v(-7.53, -310.2) * mm});
            skSolve(sketch);
        }
        {
            var Q0;
            Q0=makeQuery(id+"F33.imprint","IMPRINT",FACE,{"disambiguationData":[TD([[makeQuery(id+"F33.imprint","IMPRINT",EDGE,{"derivedFrom":sQuery(id+"F33.wireOp",EDGE,"E222.0")}),-1.0]])]});
            var Q1;
            Q1=makeQuery(id+"F33.imprint","IMPRINT",FACE,{"disambiguationData":[TD([[makeQuery(id+"F33.imprint","IMPRINT",EDGE,{"derivedFrom":sQuery(id+"F33.wireOp",EDGE,"E223.0")}),-1.0]])]});
            var Q2;
            Q2=makeQuery(id+"F33.imprint","IMPRINT",FACE,{"disambiguationData":[TD([[makeQuery(id+"F33.imprint","IMPRINT",EDGE,{"derivedFrom":sQuery(id+"F33.wireOp",EDGE,"E226.0")}),-1.0]])]});
            var Q3;
            Q3=makeQuery(id+"F33.imprint","IMPRINT",FACE,{"disambiguationData":[TD([[makeQuery(id+"F33.imprint","IMPRINT",EDGE,{"derivedFrom":sQuery(id+"F33.wireOp",EDGE,"E225.0")}),-1.0]])]});
            var Q4;
            Q4=makeQuery(id+"F33.imprint","IMPRINT",FACE,{"disambiguationData":[TD([[makeQuery(id+"F33.imprint","IMPRINT",EDGE,{"derivedFrom":sQuery(id+"F33.wireOp",EDGE,"E224.0")}),-1.0]])]});
            var Q5;
            Q5=makeQuery(id+"F33.imprint","IMPRINT",FACE,{"disambiguationData":[TD([[makeQuery(id+"F33.imprint","IMPRINT",EDGE,{"derivedFrom":sQuery(id+"F33.wireOp",EDGE,"E221.0")}),-1.0]])]});
            extrude(context, id + "F34", {"entities" : qUnion([Q0, Q1, Q2, Q3, Q4, Q5]), "operationType" : NewBodyOperationType.ADD, "depth" : 0.76 * mm, "offsetDistance" : 25.4 * mm});
        }
        {
            var Q0;
            Q0=makeQuery(id+"F34.opExtrude","SWEPT_FACE",FACE,{"disambiguationData":[OSD([sQuery(id+"F33.wireOp",EDGE,"E233")])]});
            var sketch = newSketch(context, id + "F35", { "sketchPlane" : qUnion([Q0])});
            skCircle(sketch, "E257", {"center": v(330.8, -4.99) * mm, "radius": 0.58 * mm});
            skCircle(sketch, "E258", {"center": v(319.9, -4.99) * mm, "radius": 0.58 * mm});
            skCircle(sketch, "E259", {"center": v(309.13, -4.99) * mm, "radius": 0.58 * mm});
            skSolve(sketch);
        }
        {
            var Q0;
            {var subQ0=sQuery(id+"F35.wireOp",EDGE,"E257");var subQ1=makeQuery(id+"F34.opExtrude","CAP_EDGE",EDGE,{"disambiguationData":[OSD([sQuery(id+"F33.wireOp",EDGE,"E233")])],"isStart":false});var subQ2=makeQuery(id+"F35.imprint","INTERSECT",VERTEX,{"disambiguationData":[OD(0.0)],"derivedFrom":[subQ1,subQ0]});Q0=makeQuery(id+"F35.imprint","IMPRINT",FACE,{"disambiguationData":[TD([[makeQuery(id+"F35.imprint","IMPRINT",EDGE,{"disambiguationData":[TD([[subQ2,1.0]])],"derivedFrom":subQ0}),1.0]])]});}
            var Q1;
            {var subQ0=sQuery(id+"F35.wireOp",EDGE,"E257");var subQ1=makeQuery(id+"F34.opExtrude","CAP_EDGE",EDGE,{"disambiguationData":[OSD([sQuery(id+"F33.wireOp",EDGE,"E233")])],"isStart":false});var subQ2=makeQuery(id+"F35.imprint","INTERSECT",VERTEX,{"disambiguationData":[OD(0.0)],"derivedFrom":[subQ1,subQ0]});Q1=makeQuery(id+"F35.imprint","IMPRINT",FACE,{"disambiguationData":[TD([[makeQuery(id+"F35.imprint","IMPRINT",EDGE,{"disambiguationData":[TD([[subQ2,-1.0]])],"derivedFrom":subQ0}),1.0]])]});}
            var Q2;
            Q2=makeQuery(id+"F35.imprint","IMPRINT",FACE,{"disambiguationData":[TD([[makeQuery(id+"F35.imprint","IMPRINT",EDGE,{"derivedFrom":sQuery(id+"F35.wireOp",EDGE,"E258")}),1.0]])]});
            var Q3;
            Q3=makeQuery(id+"F35.imprint","IMPRINT",FACE,{"disambiguationData":[TD([[makeQuery(id+"F35.imprint","IMPRINT",EDGE,{"derivedFrom":sQuery(id+"F35.wireOp",EDGE,"E259")}),1.0]])]});
            extrude(context, id + "F36", {"entities" : qUnion([Q0, Q1, Q2, Q3]), "operationType" : NewBodyOperationType.ADD, "depth" : 7.62 * mm, "offsetDistance" : 25.4 * mm});
        }
        {
            var Q0;
            Q0=makeQuery(id+"F36.opExtrude","CAP_FACE",FACE,{"disambiguationData":[OSD([sQuery(id+"F35.wireOp",EDGE,"E257")])],"isStart":true});
            var Q1;
            Q1=makeQuery(id+"F36.opExtrude","CAP_FACE",FACE,{"disambiguationData":[OSD([sQuery(id+"F35.wireOp",EDGE,"E258")])],"isStart":true});
            var Q2;
            Q2=makeQuery(id+"F36.opExtrude","CAP_FACE",FACE,{"disambiguationData":[OSD([sQuery(id+"F35.wireOp",EDGE,"E259")])],"isStart":true});
            extrude(context, id + "F37", {"entities" : qUnion([Q0, Q1, Q2]), "operationType" : NewBodyOperationType.ADD, "depth" : 2.54 * mm, "offsetDistance" : 25.4 * mm});
        }
        {
            var Q0;
            Q0=makeQuery(id+"F34.opExtrude","SWEPT_FACE",FACE,{"disambiguationData":[OSD([sQuery(id+"F33.wireOp",EDGE,"E245")])]});
            var sketch = newSketch(context, id + "F38", { "sketchPlane" : qUnion([Q0])});
            skArc(sketch, "E260.0", {"start": v(-330.28, -4.73) * mm, "mid": v(-330.8, -5.57) * mm, "end": v(-331.33, -4.73) * mm});
            skCircle(sketch, "E261", {"center": v(-330.8, -4.99) * mm, "radius": 0.58 * mm});
            skArc(sketch, "E262.0", {"start": v(-319.46, -4.68) * mm, "mid": v(-319.98, -5.51) * mm, "end": v(-320.5, -4.68) * mm});
            skCircle(sketch, "E263", {"center": v(-319.98, -4.93) * mm, "radius": 0.58 * mm});
            skArc(sketch, "E264.0", {"start": v(-308.54, -4.6) * mm, "mid": v(-309.06, -5.43) * mm, "end": v(-309.59, -4.6) * mm});
            skCircle(sketch, "E265", {"center": v(-309.06, -4.85) * mm, "radius": 0.58 * mm});
            skSolve(sketch);
        }
        {
            var Q0;
            Q0=makeQuery(id+"F38.imprint","IMPRINT",FACE,{"disambiguationData":[TD([[makeQuery(id+"F38.imprint","IMPRINT",EDGE,{"derivedFrom":sQuery(id+"F38.wireOp",EDGE,"E265")}),1.0]])]});
            var Q1;
            Q1=makeQuery(id+"F38.imprint","IMPRINT",FACE,{"disambiguationData":[TD([[makeQuery(id+"F38.imprint","IMPRINT",EDGE,{"derivedFrom":sQuery(id+"F38.wireOp",EDGE,"E263")}),1.0]])]});
            var Q2;
            {var subQ0=sQuery(id+"F38.wireOp",EDGE,"E261");var subQ1=makeQuery(id+"F34.opExtrude","CAP_EDGE",EDGE,{"disambiguationData":[OSD([sQuery(id+"F33.wireOp",EDGE,"E245")])],"isStart":false});var subQ2=makeQuery(id+"F38.imprint","INTERSECT",VERTEX,{"disambiguationData":[OD(0.0)],"derivedFrom":[subQ1,subQ0]});Q2=makeQuery(id+"F38.imprint","IMPRINT",FACE,{"disambiguationData":[TD([[makeQuery(id+"F38.imprint","IMPRINT",EDGE,{"disambiguationData":[TD([[subQ2,1.0]])],"derivedFrom":subQ0}),1.0]])]});}
            var Q3;
            {var subQ0=sQuery(id+"F38.wireOp",EDGE,"E261");var subQ1=makeQuery(id+"F34.opExtrude","CAP_EDGE",EDGE,{"disambiguationData":[OSD([sQuery(id+"F33.wireOp",EDGE,"E245")])],"isStart":false});var subQ2=makeQuery(id+"F38.imprint","INTERSECT",VERTEX,{"disambiguationData":[OD(0.0)],"derivedFrom":[subQ1,subQ0]});Q3=makeQuery(id+"F38.imprint","IMPRINT",FACE,{"disambiguationData":[TD([[makeQuery(id+"F38.imprint","IMPRINT",EDGE,{"disambiguationData":[TD([[subQ2,-1.0]])],"derivedFrom":subQ0}),1.0]])]});}
            extrude(context, id + "F39", {"entities" : qUnion([Q0, Q1, Q2, Q3]), "operationType" : NewBodyOperationType.ADD, "depth" : 7.62 * mm, "offsetDistance" : 25.4 * mm});
        }
        {
            var Q0;
            Q0=makeQuery(id+"F39.opExtrude","CAP_FACE",FACE,{"disambiguationData":[OSD([sQuery(id+"F38.wireOp",EDGE,"E261")])],"isStart":true});
            var Q1;
            Q1=makeQuery(id+"F39.opExtrude","CAP_FACE",FACE,{"disambiguationData":[OSD([sQuery(id+"F38.wireOp",EDGE,"E263")])],"isStart":true});
            var Q2;
            Q2=makeQuery(id+"F39.opExtrude","CAP_FACE",FACE,{"disambiguationData":[OSD([sQuery(id+"F38.wireOp",EDGE,"E265")])],"isStart":true});
            extrude(context, id + "F40", {"entities" : qUnion([Q0, Q1, Q2]), "operationType" : NewBodyOperationType.ADD, "depth" : 2.54 * mm, "offsetDistance" : 25.4 * mm});
        }
        {
            var Q0;
            Q0=makeQuery(id+"F36.opExtrude","CAP_FACE",FACE,{"disambiguationData":[OSD([sQuery(id+"F35.wireOp",EDGE,"E257")])],"isStart":false});
            var sketch = newSketch(context, id + "F41", { "sketchPlane" : qUnion([Q0])});
            skLineSegment(sketch, "E266", {"start": v(330.76, -4.28) * mm, "end": v(329.98, -4.28) * mm});
            skLineSegment(sketch, "E267", {"start": v(329.98, -4.28) * mm, "end": v(328.8, -4.73) * mm});
            skLineSegment(sketch, "E268", {"start": v(328.8, -4.73) * mm, "end": v(328.8, -5.23) * mm});
            skLineSegment(sketch, "E269", {"start": v(328.8, -5.23) * mm, "end": v(329.98, -5.63) * mm});
            skLineSegment(sketch, "E270", {"start": v(329.98, -5.63) * mm, "end": v(330.76, -5.63) * mm});
            skLineSegment(sketch, "E271", {"start": v(330.76, -5.63) * mm, "end": v(330.76, -4.28) * mm, "construction": true});
            skLineSegment(sketch, "E272.MirrorCS", {"start": v(332.73, -5.23) * mm, "end": v(331.54, -5.63) * mm});
            skLineSegment(sketch, "E273.MirrorCS", {"start": v(332.73, -4.73) * mm, "end": v(332.73, -5.23) * mm});
            skLineSegment(sketch, "E274.MirrorCS", {"start": v(331.54, -4.28) * mm, "end": v(332.73, -4.73) * mm});
            skLineSegment(sketch, "E275.MirrorCS", {"start": v(330.76, -4.28) * mm, "end": v(331.54, -4.28) * mm});
            skLineSegment(sketch, "E276.MirrorCS", {"start": v(331.54, -5.63) * mm, "end": v(330.76, -5.63) * mm});
            skLineSegment(sketch, "E277", {"start": v(319.87, -4.35) * mm, "end": v(319.1, -4.35) * mm});
            skLineSegment(sketch, "E278", {"start": v(319.1, -4.35) * mm, "end": v(317.9, -4.8) * mm});
            skLineSegment(sketch, "E279", {"start": v(317.9, -4.8) * mm, "end": v(317.9, -5.3) * mm});
            skLineSegment(sketch, "E280", {"start": v(317.9, -5.3) * mm, "end": v(319.1, -5.7) * mm});
            skLineSegment(sketch, "E281", {"start": v(319.1, -5.7) * mm, "end": v(319.87, -5.7) * mm});
            skLineSegment(sketch, "E282", {"start": v(319.87, -5.7) * mm, "end": v(319.87, -4.35) * mm, "construction": true});
            skLineSegment(sketch, "E283.MirrorCS", {"start": v(321.84, -5.3) * mm, "end": v(320.65, -5.7) * mm});
            skLineSegment(sketch, "E284.MirrorCS", {"start": v(321.84, -4.8) * mm, "end": v(321.84, -5.3) * mm});
            skLineSegment(sketch, "E285.MirrorCS", {"start": v(320.65, -4.35) * mm, "end": v(321.84, -4.8) * mm});
            skLineSegment(sketch, "E286.MirrorCS", {"start": v(319.87, -4.35) * mm, "end": v(320.65, -4.35) * mm});
            skLineSegment(sketch, "E287.MirrorCS", {"start": v(320.65, -5.7) * mm, "end": v(319.87, -5.7) * mm});
            skLineSegment(sketch, "E288", {"start": v(309.06, -4.29) * mm, "end": v(308.29, -4.29) * mm});
            skLineSegment(sketch, "E289", {"start": v(308.29, -4.29) * mm, "end": v(307.1, -4.74) * mm});
            skLineSegment(sketch, "E290", {"start": v(307.1, -4.74) * mm, "end": v(307.1, -5.24) * mm});
            skLineSegment(sketch, "E291", {"start": v(307.1, -5.24) * mm, "end": v(308.29, -5.64) * mm});
            skLineSegment(sketch, "E292", {"start": v(308.29, -5.64) * mm, "end": v(309.06, -5.64) * mm});
            skLineSegment(sketch, "E293", {"start": v(309.06, -5.64) * mm, "end": v(309.06, -4.29) * mm, "construction": true});
            skLineSegment(sketch, "E294.MirrorCS", {"start": v(311.03, -5.24) * mm, "end": v(309.84, -5.64) * mm});
            skLineSegment(sketch, "E295.MirrorCS", {"start": v(311.03, -4.74) * mm, "end": v(311.03, -5.24) * mm});
            skLineSegment(sketch, "E296.MirrorCS", {"start": v(309.84, -4.29) * mm, "end": v(311.03, -4.74) * mm});
            skLineSegment(sketch, "E297.MirrorCS", {"start": v(309.06, -4.29) * mm, "end": v(309.84, -4.29) * mm});
            skLineSegment(sketch, "E298.MirrorCS", {"start": v(309.84, -5.64) * mm, "end": v(309.06, -5.64) * mm});
            skSolve(sketch);
        }
        {
            var Q0;
            Q0=makeQuery(id+"F41.imprint","IMPRINT",FACE,{"disambiguationData":[TD([[makeQuery(id+"F41.imprint","IMPRINT",EDGE,{"derivedFrom":sQuery(id+"F41.wireOp",EDGE,"E288")}),1.0]])]});
            var Q1;
            Q1=makeQuery(id+"F41.imprint","IMPRINT",FACE,{"disambiguationData":[TD([[makeQuery(id+"F41.imprint","IMPRINT",EDGE,{"derivedFrom":sQuery(id+"F41.wireOp",EDGE,"E277")}),1.0]])]});
            var Q2;
            Q2=makeQuery(id+"F41.imprint","IMPRINT",FACE,{"disambiguationData":[TD([[makeQuery(id+"F41.imprint","IMPRINT",EDGE,{"derivedFrom":sQuery(id+"F41.wireOp",EDGE,"E266")}),1.0]])]});
            var Q3;
            Q3=makeQuery(id+"F41.imprint","IMPRINT",FACE,{"disambiguationData":[TD([[makeQuery(id+"F41.imprint","IMPRINT",EDGE,{"derivedFrom":makeQuery(id+"F36.opExtrude","CAP_EDGE",EDGE,{"disambiguationData":[OSD([sQuery(id+"F35.wireOp",EDGE,"E257")])],"isStart":false})}),1.0]])]});
            extrude(context, id + "F42", {"entities" : qUnion([Q0, Q1, Q2, Q3]), "operationType" : NewBodyOperationType.ADD, "depth" : 2.54 * mm, "offsetDistance" : 25.4 * mm});
        }
        {
            var Q0;
            Q0=makeQuery(id+"F39.opExtrude","CAP_FACE",FACE,{"disambiguationData":[OSD([sQuery(id+"F38.wireOp",EDGE,"E261")])],"isStart":false});
            var sketch = newSketch(context, id + "F43", { "sketchPlane" : qUnion([Q0])});
            skLineSegment(sketch, "E299", {"start": v(-330.82, -4.25) * mm, "end": v(-331.6, -4.25) * mm});
            skLineSegment(sketch, "E300", {"start": v(-331.6, -4.25) * mm, "end": v(-332.78, -4.7) * mm});
            skLineSegment(sketch, "E301", {"start": v(-332.78, -4.7) * mm, "end": v(-332.78, -5.2) * mm});
            skLineSegment(sketch, "E302", {"start": v(-332.78, -5.2) * mm, "end": v(-331.6, -5.6) * mm});
            skLineSegment(sketch, "E303", {"start": v(-331.6, -5.6) * mm, "end": v(-330.82, -5.6) * mm});
            skLineSegment(sketch, "E304", {"start": v(-330.82, -5.6) * mm, "end": v(-330.82, -4.25) * mm, "construction": true});
            skLineSegment(sketch, "E305.MirrorCS", {"start": v(-328.85, -5.2) * mm, "end": v(-330.04, -5.6) * mm});
            skLineSegment(sketch, "E306.MirrorCS", {"start": v(-328.85, -4.7) * mm, "end": v(-328.85, -5.2) * mm});
            skLineSegment(sketch, "E307.MirrorCS", {"start": v(-330.04, -4.25) * mm, "end": v(-328.85, -4.7) * mm});
            skLineSegment(sketch, "E308.MirrorCS", {"start": v(-330.82, -4.25) * mm, "end": v(-330.04, -4.25) * mm});
            skLineSegment(sketch, "E309.MirrorCS", {"start": v(-330.04, -5.6) * mm, "end": v(-330.82, -5.6) * mm});
            skLineSegment(sketch, "E310", {"start": v(-320.02, -4.27) * mm, "end": v(-320.8, -4.27) * mm});
            skLineSegment(sketch, "E311", {"start": v(-320.8, -4.27) * mm, "end": v(-322, -4.72) * mm});
            skLineSegment(sketch, "E312", {"start": v(-322, -4.72) * mm, "end": v(-322, -5.22) * mm});
            skLineSegment(sketch, "E313", {"start": v(-322, -5.22) * mm, "end": v(-320.8, -5.62) * mm});
            skLineSegment(sketch, "E314", {"start": v(-320.8, -5.62) * mm, "end": v(-320.02, -5.62) * mm});
            skLineSegment(sketch, "E315", {"start": v(-320.02, -5.62) * mm, "end": v(-320.02, -4.27) * mm, "construction": true});
            skLineSegment(sketch, "E316.MirrorCS", {"start": v(-318.06, -5.22) * mm, "end": v(-319.25, -5.62) * mm});
            skLineSegment(sketch, "E317.MirrorCS", {"start": v(-318.06, -4.72) * mm, "end": v(-318.06, -5.22) * mm});
            skLineSegment(sketch, "E318.MirrorCS", {"start": v(-319.25, -4.27) * mm, "end": v(-318.06, -4.72) * mm});
            skLineSegment(sketch, "E319.MirrorCS", {"start": v(-320.02, -4.27) * mm, "end": v(-319.25, -4.27) * mm});
            skLineSegment(sketch, "E320.MirrorCS", {"start": v(-319.25, -5.62) * mm, "end": v(-320.02, -5.62) * mm});
            skLineSegment(sketch, "E321", {"start": v(-309.08, -4.25) * mm, "end": v(-309.86, -4.25) * mm});
            skLineSegment(sketch, "E322", {"start": v(-309.86, -4.25) * mm, "end": v(-311.05, -4.7) * mm});
            skLineSegment(sketch, "E323", {"start": v(-311.05, -4.7) * mm, "end": v(-311.05, -5.2) * mm});
            skLineSegment(sketch, "E324", {"start": v(-311.05, -5.2) * mm, "end": v(-309.86, -5.6) * mm});
            skLineSegment(sketch, "E325", {"start": v(-309.86, -5.6) * mm, "end": v(-309.08, -5.6) * mm});
            skLineSegment(sketch, "E326", {"start": v(-309.08, -5.6) * mm, "end": v(-309.08, -4.25) * mm, "construction": true});
            skLineSegment(sketch, "E327.MirrorCS", {"start": v(-307.11, -5.2) * mm, "end": v(-308.3, -5.6) * mm});
            skLineSegment(sketch, "E328.MirrorCS", {"start": v(-307.11, -4.7) * mm, "end": v(-307.11, -5.2) * mm});
            skLineSegment(sketch, "E329.MirrorCS", {"start": v(-308.3, -4.25) * mm, "end": v(-307.11, -4.7) * mm});
            skLineSegment(sketch, "E330.MirrorCS", {"start": v(-309.08, -4.25) * mm, "end": v(-308.3, -4.25) * mm});
            skLineSegment(sketch, "E331.MirrorCS", {"start": v(-308.3, -5.6) * mm, "end": v(-309.08, -5.6) * mm});
            skSolve(sketch);
        }
        {
            var Q0;
            Q0=makeQuery(id+"F43.imprint","IMPRINT",FACE,{"disambiguationData":[TD([[makeQuery(id+"F43.imprint","IMPRINT",EDGE,{"derivedFrom":sQuery(id+"F43.wireOp",EDGE,"E321")}),1.0]])]});
            var Q1;
            Q1=makeQuery(id+"F43.imprint","IMPRINT",FACE,{"disambiguationData":[TD([[makeQuery(id+"F43.imprint","IMPRINT",EDGE,{"derivedFrom":sQuery(id+"F43.wireOp",EDGE,"E310")}),1.0]])]});
            var Q2;
            Q2=makeQuery(id+"F43.imprint","IMPRINT",FACE,{"disambiguationData":[TD([[makeQuery(id+"F43.imprint","IMPRINT",EDGE,{"derivedFrom":sQuery(id+"F43.wireOp",EDGE,"E299")}),1.0]])]});
            var Q3;
            Q3=makeQuery(id+"F43.imprint","IMPRINT",FACE,{"disambiguationData":[TD([[makeQuery(id+"F43.imprint","IMPRINT",EDGE,{"derivedFrom":makeQuery(id+"F39.opExtrude","CAP_EDGE",EDGE,{"disambiguationData":[OSD([sQuery(id+"F38.wireOp",EDGE,"E261")])],"isStart":false})}),1.0]])]});
            extrude(context, id + "F44", {"entities" : qUnion([Q0, Q1, Q2, Q3]), "operationType" : NewBodyOperationType.ADD, "depth" : 2.54 * mm, "offsetDistance" : 25.4 * mm});
        }
        {
            var Q0;
            Q0=makeQuery(id+"F22.opExtrude","CAP_FACE",FACE,{"disambiguationData":[OSD([sQuery(id+"F21.wireOp",EDGE,"E79"),sQuery(id+"F21.wireOp",EDGE,"E80"),sQuery(id+"F21.wireOp",EDGE,"E81"),sQuery(id+"F21.wireOp",EDGE,"E82")])],"isStart":false});
            var sketch = newSketch(context, id + "F45", { "sketchPlane" : qUnion([Q0])});
            skLineSegment(sketch, "E332", {"start": v(-8.79, 294.68) * mm, "end": v(-8.79, -10.62) * mm});
            skLineSegment(sketch, "E333", {"start": v(-5.75, 294.68) * mm, "end": v(-5.75, -10.62) * mm});
            skLineSegment(sketch, "E334", {"start": v(-2.8, 294.68) * mm, "end": v(-2.8, -10.62) * mm});
            skLineSegment(sketch, "E335", {"start": v(0, 294.68) * mm, "end": v(0, -10.62) * mm});
            skLineSegment(sketch, "E336", {"start": v(4.2, 294.68) * mm, "end": v(4.2, -10.62) * mm});
            skLineSegment(sketch, "E337", {"start": v(7.85, 294.68) * mm, "end": v(7.85, -10.62) * mm});
            skSolve(sketch);
        }
        {
            var Q0;
            Q0=sQuery(id+"F45.wireOp",EDGE,"E337");
            var Q1;
            Q1=sQuery(id+"F45.wireOp",EDGE,"E336");
            var Q2;
            Q2=sQuery(id+"F45.wireOp",EDGE,"E335");
            var Q3;
            Q3=sQuery(id+"F45.wireOp",EDGE,"E334");
            var Q4;
            Q4=sQuery(id+"F45.wireOp",EDGE,"E333");
            var Q5;
            Q5=sQuery(id+"F45.wireOp",EDGE,"E332");
            extrude(context, id + "F46", {"bodyType" : ToolBodyType.SURFACE, "surfaceEntities" : qUnion([Q0, Q1, Q2, Q3, Q4, Q5]), "depth" : 0.5 * mm, "offsetDistance" : 25.4 * mm});
        }
    });
